# Revit family: REVIT-MXO-2017
name_source: partatom
category: Mechanical Equipment
revit_build: Autodesk Revit 2017 (Build: 20190507_1515(x64)
units: mm (PartAtom-declared; Revit-internal decimal feet)

## family parameters
Always vertical = Yes
Cut with Voids When Loaded = No
Part Type = Normal
Room Calculation Point = No
Round Connector Dimension = Use Radius
Shared = No
Work Plane-Based = No

## types (1)
- REVIT-MXO-2017
    A = 8 3/8"
    Air Inlet Depth = 3 1/8"
    Air Inlet Diameter = 6"
    Air Inlet Extension = 18 15/16"
    Air Inlet Radius = 3"
    Air Inlet Width = 6 3/8"
    Air Inlet X = 14 7/8"
    Air Inlet Y = 5 1/4"
    Air Inlet Y Offset = 2 1/16"
    Air Inlet Z Offset = 2 1/16"
    Assembly Code = D3040400
    B = 3 15/16"
    Blower Motor Current = 8 A
    Blower Motor HP = 0.3333
    Blower Motor Phase = 1
    Blower Motor Voltage = 120 V
    Burner Depth = 16 1/2"
    Burner Height = 13 3/4"
    Burner Width = 14 11/16"
    Cold Water Extension = 18 1/8"
    Cold Water NPT = 2"
    Cold Water Radius = 1"
    Control Panel Extension = 24 1/8"
    Controls = 2 A
    Description = Maxim Series Oil Water Heater
    Disclaimer = This rendering is for building modeling purposes only. Submittal/catalog is still the contract document. PVI reserves the right to change design and specification without notice.
    Drain Extension = 21"
    Drain NPT = 1"
    Drain Radius = 1/2"
    Energy Extension = 19 5/8"
    Energy Radius = 4"
    Flue Diameter = 7"
    Flue Radius = 3 1/2"
    Frequency = 60 Hz
    Height to Cold Inlet = 25"
    Height to Drain = 25 1/2"
    Height to Energy = 7"
    Height to Hot Outlet = 62"
    Height to Relief = 62 5/8"
    Hot Water Extension = 18 1/8"
    Hot Water NPT = 2"
    Hot Water Radius = 1"
    Input = 140000 Btu/h
    Manufacturer = PVI Industries, LLC
    Model = 14 L 125A-MXO
    RandD Angle = 45.00°
    Rear Skid Extension = 17 1/8"
    Recovery Rate 40F to 140F = 140 gph
    Relief Extension = 20 1/8"
    Relief Valve NPT = 1"
    Relief Valve Radius = 1/2"
    Skid Center Dist = 10 1/4"
    Skid Length = 34 1/2"
    Skid Spacing = 20 1/2"
    URL = www.pvi.com
    Unit Height = 72"
    Unit Radius = 17 1/8"
    Weight = 1020

## geometry (parser evidence)
native form markers: Blend x2, Sweep x3
no freeform markers — native parametric forms only
